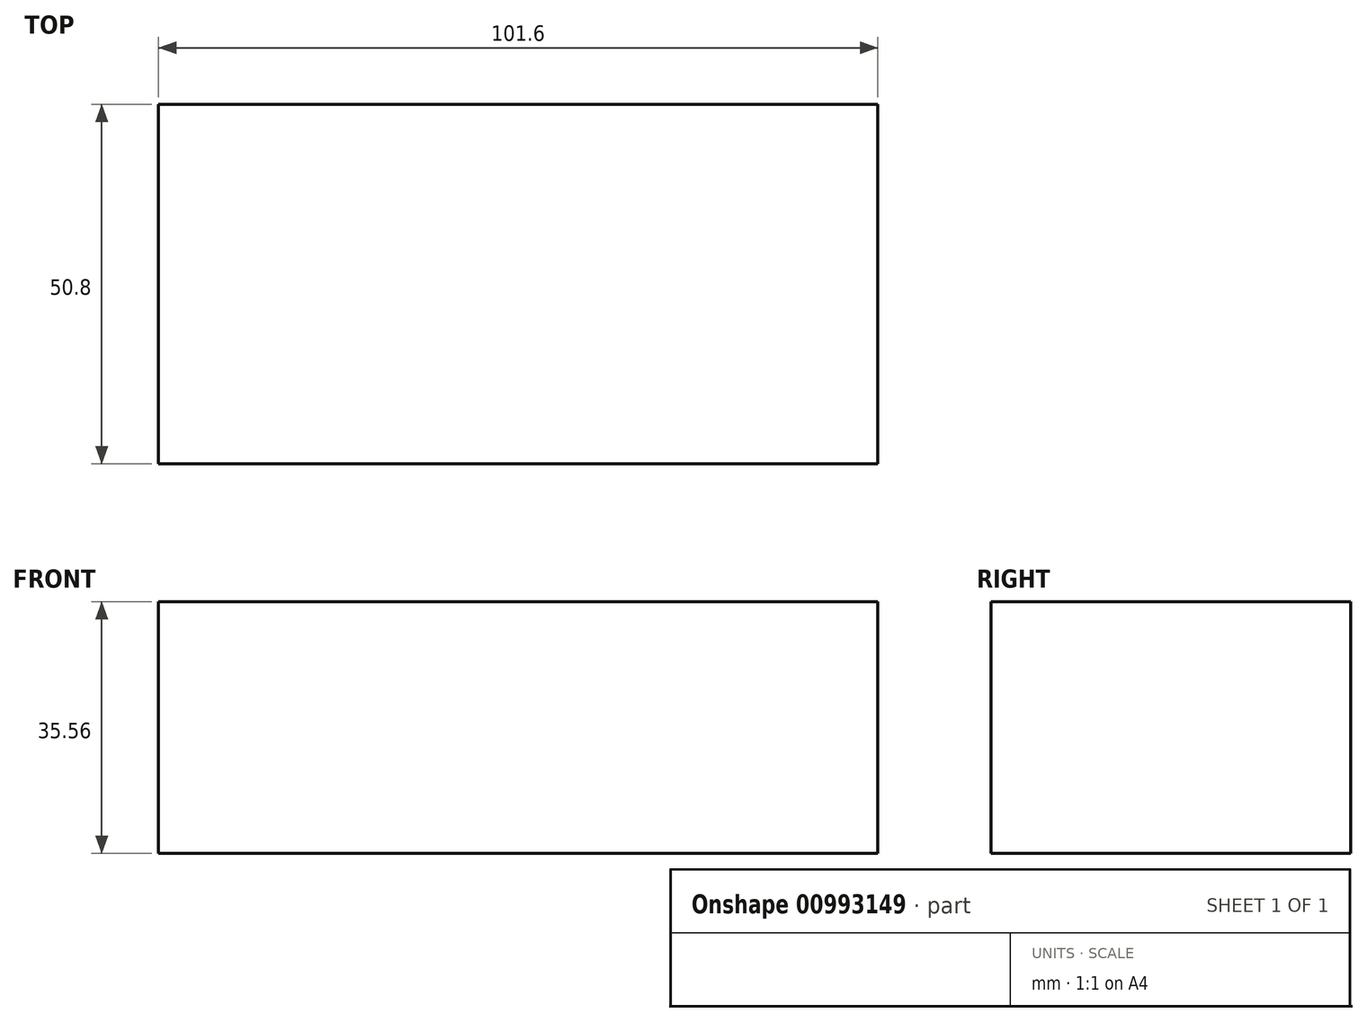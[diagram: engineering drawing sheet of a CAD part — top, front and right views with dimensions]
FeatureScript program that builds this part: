
annotation { "Feature Type Name" : "Feature", "Feature Type Description" : "" }
export const myFeature = defineFeature(function(context is Context, id is Id, definition is map)
    precondition{}
    {
        {
            var Q0;
            Q0=qCreatedBy(makeId("Front.planeOp"),FACE);
            var sketch = newSketch(context, id + "F0", { "sketchPlane" : qUnion([Q0])});
            skLineSegment(sketch, "E0.bottom", {"start": v(-60.39, 49.06) * mm, "end": v(41.21, 49.06) * mm});
            skLineSegment(sketch, "E0.top", {"start": v(-60.39, 13.5) * mm, "end": v(41.21, 13.5) * mm});
            skLineSegment(sketch, "E0.left", {"start": v(-60.39, 49.06) * mm, "end": v(-60.39, 13.5) * mm});
            skLineSegment(sketch, "E0.right", {"start": v(41.21, 49.06) * mm, "end": v(41.21, 13.5) * mm});
            skSolve(sketch);
        }
        {
            var Q0;
            Q0=makeQuery(id+"F0.imprint","IMPRINT",FACE,{"disambiguationData":[TD([[makeQuery(id+"F0.imprint","IMPRINT",EDGE,{"derivedFrom":sQuery(id+"F0.wireOp",EDGE,"E0.bottom")}),-1.0]])]});
            extrude(context, id + "F1", {"entities" : qUnion([Q0]), "depth" : 50.8 * mm, "offsetDistance" : 25.4 * mm});
        }
    });
